# Revit family: 500_Slenderline_Sliding_Window_XXXX_Custom
name_source: partatom
category: Windows
revit_build: Autodesk Revit 2014 (Build: 20130308_1515(x64)
units: mm (PartAtom-declared; Revit-internal decimal feet)

## types (1)
- 500SW-XXXX-Custom
    Area Middle Sash Glazing = 0.59 m²
    Area Side Sash Glazing = 0.59 m²
    Astragal Sash Gap = 1 mm  [stored 0.00328084 ft]
    Centered In Wall = Yes
    Custom Frame Offset From Exterior = 0 mm  [stored 0 ft]
    Custom SHGC Value = 0
    Custom Sash Width Side = 800 mm
    Custom Windload = 1000 mm  [stored 3.28084 ft]
    Custom Window Height = 1200 mm
    Custom Window Width = 2400 mm
    Default Sill Height = 800 mm
    Description = Slenderline Sliding Window
    Equal Sash Width = Yes
    Frame Thickness = 54 mm
    Heavy Duty Handle = No
    Heavy Duty Handle Gap = 27 mm
    Heavy Duty Interlocker = No
    Height = 1200 mm
    Is Heavy Duty Handle = 0 mm  [stored 0 ft]
    Is Heavy Duty Mullion = 0 mm  [stored 0 ft]
    Limit Sash Height Max = 1500 mm
    Limit Sash Height Min = 300 mm  [stored 0.984252 ft]
    Limit Sash Width Max = 750 mm
    Limit Sash Width Min = 300 mm  [stored 0.984252 ft]
    Limit Sash Width Side Max = 750 mm
    Limit Sash Width Side Min = 438 mm
    Limit Window Height Max = 1575 mm
    Limit Window Height Min = 375 mm
    Limit Window Width Max = 3024 mm
    Limit Window Width Min = 1224 mm
    Manufacturer = Crealco
    Max Pane Area = 0.59 m²
    Model = 500
    Sash Frame Seal = 1 mm  [stored 0.00328084 ft]
    Sash Height = 1125 mm
    Sash Rail Fore Aft Spacing = 2 mm  [stored 0.00656168 ft]
    Sash Width Middle = 594 mm
    Sash Width Sides = 594 mm
    Standard Interlocker = Yes
    URL = www.crealco.co.za
    Wall Closure = By host
    Width = 2400 mm
    Windload Design = 1000 mm  [stored 3.28084 ft]

note: [stored X ft] marks values corroborated as IEEE doubles in the binary element streams (Revit-internal decimal feet)

## geometry (parser evidence)
native form markers: Sweep x45
no freeform markers — native parametric forms only
